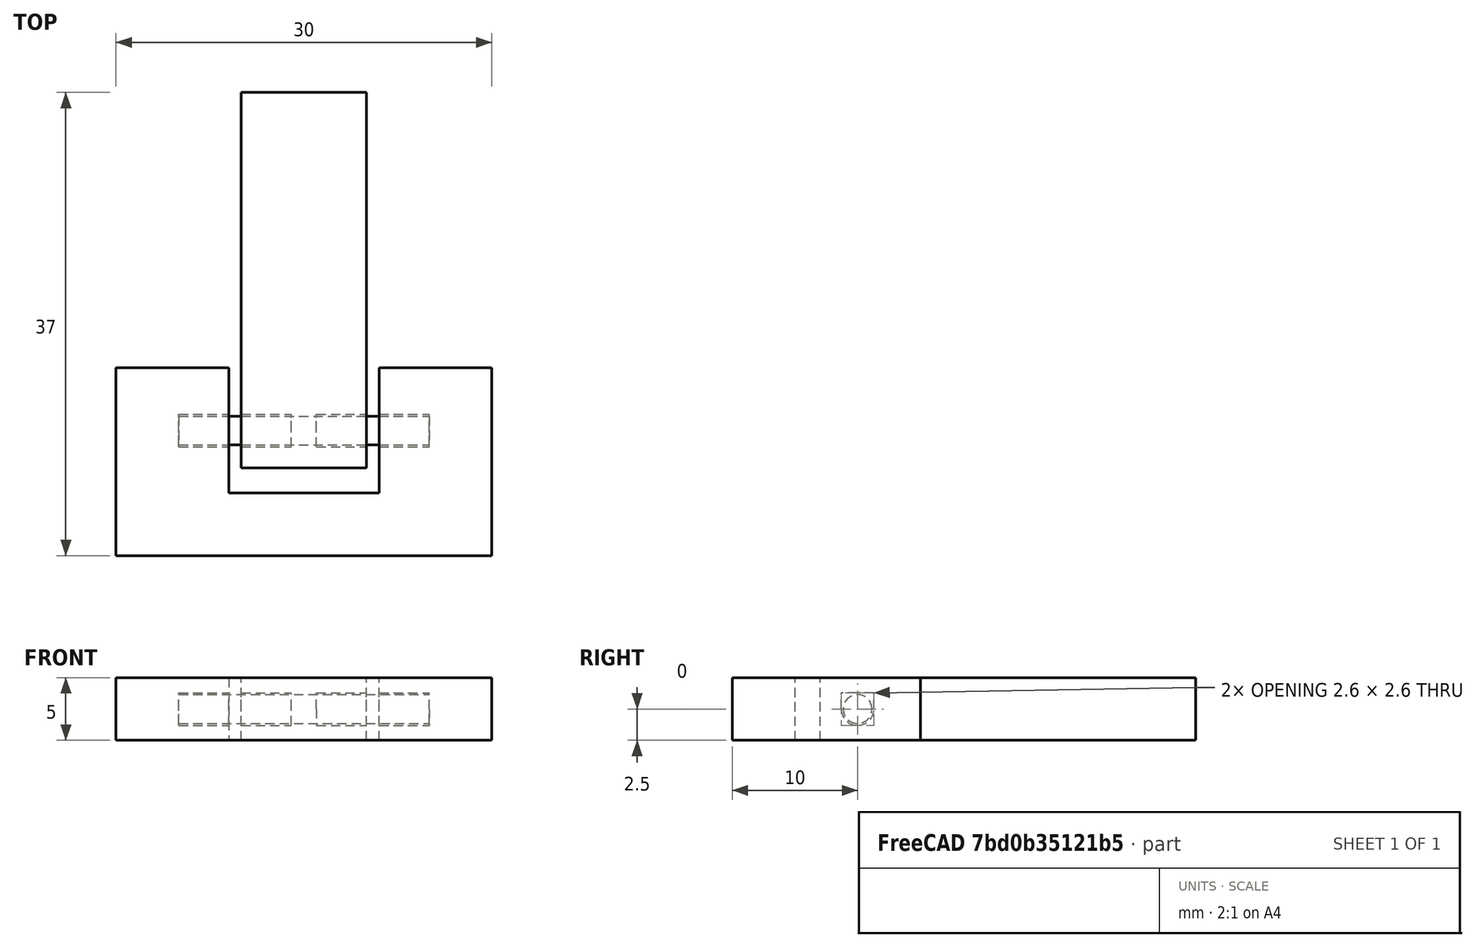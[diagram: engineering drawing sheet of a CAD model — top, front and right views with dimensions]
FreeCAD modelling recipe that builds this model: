
FCSTD DOCUMENT  (FreeCAD 0.16R)
Label: Hinge 0.2
License: All rights reserved
LicenseURL: http://en.wikipedia.org/wiki/All_rights_reserved
objects: Part::Box×5, Part::MultiFuse×4, Part::Cylinder×3, Part::Cut×2
note: 14 computed .brp shape members not serialized (recipe doc carries the construction recipe); baked Part::Feature solids carry a one-line shape summary decoded from their .brp

FEATURE [Part::Box] Box  label="Cube"
  Height = 5
  Length = 30
  Placement = pos=(0,-10,-2.5) rot=(0,0,1;0rad)
  Width = 15
FEATURE [Part::Box] Box001  label="Cube001"
  Height = 5
  Length = 10
  Placement = pos=(10,-3,-2.5) rot=(0,0,1;0rad)
  Width = 30
FEATURE [Part::Cylinder] Cylinder
  Angle = 360
  Height = 20
  Placement = pos=(5,0,0) rot=(0,1,0;1.5708rad)
  Radius = 1.15
FEATURE [Part::Cylinder] Cylinder001
  Angle = 360
  Height = 9
  Placement = pos=(5,0,0) rot=(0,1,0;1.5708rad)
  Radius = 1.3
FEATURE [Part::Box] Box002  label="Cube002"
  Height = 1.3
  Length = 9
  Placement = pos=(5,-1.3,0) rot=(0,0,1;0rad)
  Width = 2.6
FEATURE [Part::Box] Box003  label="Cube003"
  Height = 5
  Length = 12
  Placement = pos=(9,-5,-2.5) rot=(0,0,1;0rad)
  Width = 30
FEATURE [Part::MultiFuse] Fusion
  Shapes = -> [Cylinder001,Box002]
FEATURE [Part::Cut] Cut
  Base = -> Box
  Tool = -> Box003
FEATURE [Part::Cylinder] Cylinder002
  Angle = 360
  Height = 9
  Placement = pos=(5,0,0) rot=(0,1,0;1.5708rad)
  Radius = 1.3
FEATURE [Part::Box] Box004  label="Cube004"
  Height = 1.3
  Length = 9
  Placement = pos=(5,-1.3,0) rot=(0,0,1;0rad)
  Width = 2.6
FEATURE [Part::MultiFuse] Fusion001
  Placement = pos=(11,0,0) rot=(0,0,1;0rad)
  Shapes = -> [Cylinder002,Box004]
FEATURE [Part::MultiFuse] Fusion002
  Shapes = -> [Fusion,Fusion001]
FEATURE [Part::MultiFuse] Fusion003
  Shapes = -> [Cut,Box001]
FEATURE [Part::Cut] Cut001
  Base = -> Fusion003
  Tool = -> Fusion002
